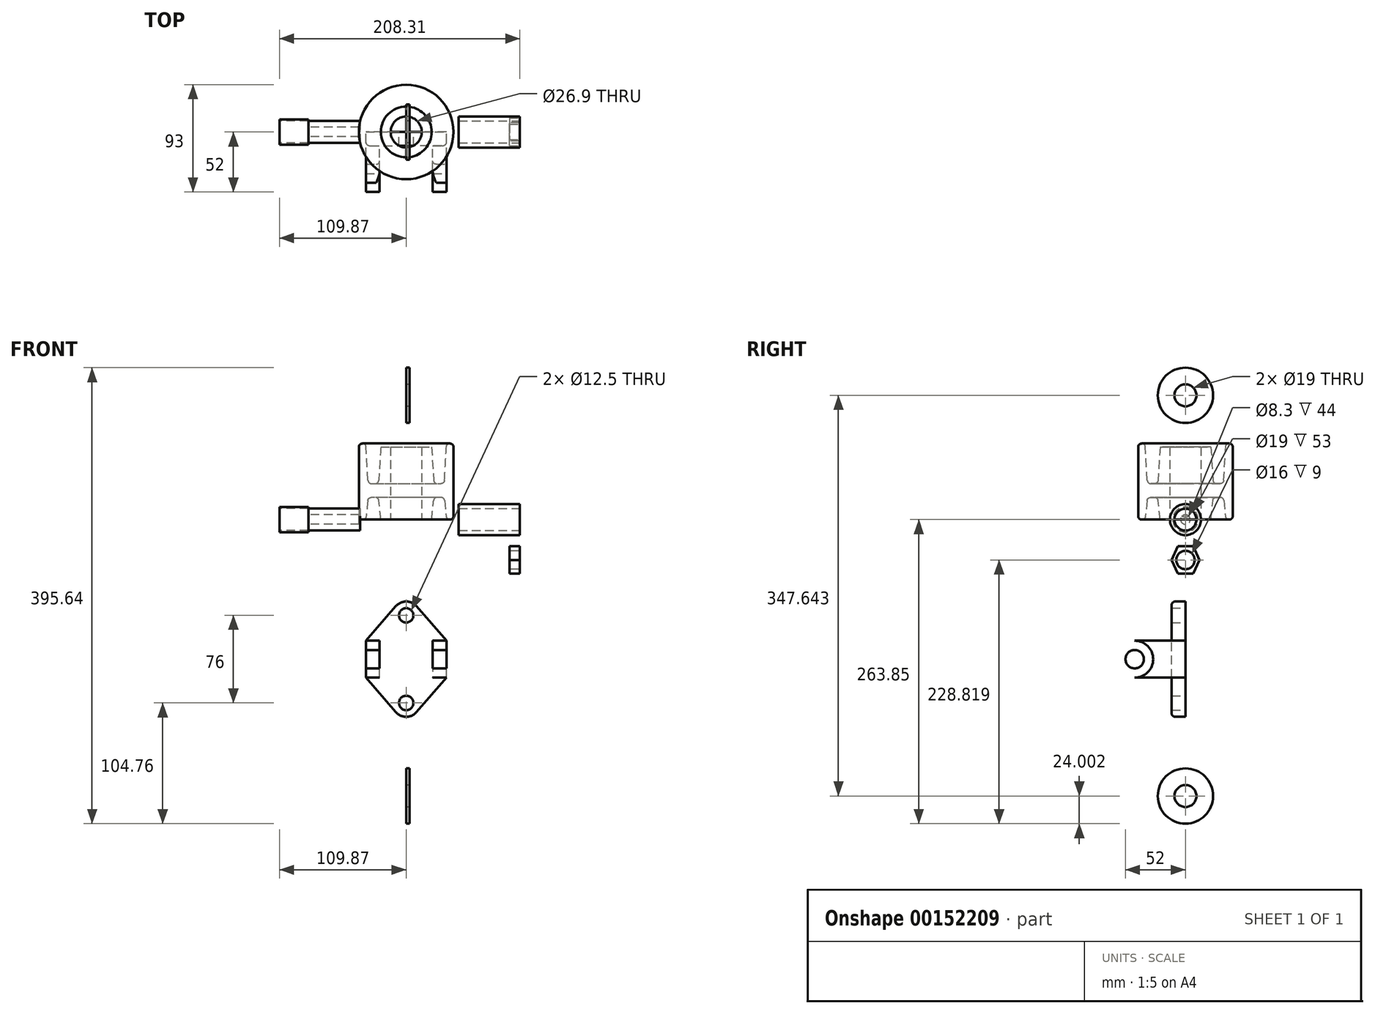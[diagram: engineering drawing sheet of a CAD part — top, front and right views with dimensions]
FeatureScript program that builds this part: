
annotation { "Feature Type Name" : "Feature", "Feature Type Description" : "" }
export const myFeature = defineFeature(function(context is Context, id is Id, definition is map)
    precondition{}
    {
        {
            var Q0;
            Q0=qCreatedBy(makeId("Front.planeOp"),FACE);
            var sketch = newSketch(context, id + "F0", { "sketchPlane" : qUnion([Q0])});
            skLineSegment(sketch, "E0", {"start": v(-13.45, 0) * mm, "end": v(-13.45, 63) * mm});
            skLineSegment(sketch, "E1", {"start": v(-13.45, 63) * mm, "end": v(-22, 63) * mm});
            skLineSegment(sketch, "E2", {"start": v(-22, 63) * mm, "end": v(-24, 31.2) * mm});
            skLineSegment(sketch, "E3", {"start": v(-24, 31.2) * mm, "end": v(-33, 31.2) * mm});
            skLineSegment(sketch, "E4", {"start": v(-33, 31.2) * mm, "end": v(-35, 66) * mm});
            skLineSegment(sketch, "E5", {"start": v(-35, 66) * mm, "end": v(-41, 66) * mm});
            skLineSegment(sketch, "E6", {"start": v(-41, 66) * mm, "end": v(-41, 0) * mm});
            skLineSegment(sketch, "E7", {"start": v(-41, 0) * mm, "end": v(-35, 0) * mm});
            skLineSegment(sketch, "E8", {"start": v(-35, 0) * mm, "end": v(-33, 19.2) * mm});
            skLineSegment(sketch, "E9", {"start": v(-33, 19.2) * mm, "end": v(-24, 19.2) * mm});
            skLineSegment(sketch, "E10", {"start": v(-24, 19.2) * mm, "end": v(-22, 0) * mm});
            skLineSegment(sketch, "E11", {"start": v(-22, 0) * mm, "end": v(-13.45, 0) * mm});
            skLineSegment(sketch, "E12", {"start": v(0, 0) * mm, "end": v(0, 72.33) * mm, "construction": true});
            skSolve(sketch);
        }
        {
            var Q0;
            Q0=qSketchRegion(id+"F0",true);
            var Q1;
            Q1=sQuery(id+"F0.wireOp",EDGE,"E12");
            revolve(context, id + "F1", {"entities" : qUnion([Q0]), "axis" : qUnion([Q1]), "revolveType" : RevolveType.FULL});
        }
        {
            var Q0;
            Q0=makeQuery(id+"F1.opRevolve","SWEPT_EDGE",EDGE,{"disambiguationData":[OSD([sQuery(id+"F0.wireOp",EDGE,"E5"),sQuery(id+"F0.wireOp",EDGE,"E6")])]});
            var Q1;
            Q1=makeQuery(id+"F1.opRevolve","SWEPT_EDGE",EDGE,{"disambiguationData":[OSD([sQuery(id+"F0.wireOp",EDGE,"E4"),sQuery(id+"F0.wireOp",EDGE,"E5")])]});
            var Q2;
            Q2=makeQuery(id+"F1.opRevolve","SWEPT_EDGE",EDGE,{"disambiguationData":[OSD([sQuery(id+"F0.wireOp",EDGE,"E2"),sQuery(id+"F0.wireOp",EDGE,"E3")])]});
            var Q3;
            Q3=makeQuery(id+"F1.opRevolve","SWEPT_FACE",FACE,{"disambiguationData":[OSD([sQuery(id+"F0.wireOp",EDGE,"E3")])]});
            var Q4;
            Q4=makeQuery(id+"F1.opRevolve","SWEPT_EDGE",EDGE,{"disambiguationData":[OSD([sQuery(id+"F0.wireOp",EDGE,"E6"),sQuery(id+"F0.wireOp",EDGE,"E7")])]});
            var Q5;
            Q5=makeQuery(id+"F1.opRevolve","SWEPT_EDGE",EDGE,{"disambiguationData":[OSD([sQuery(id+"F0.wireOp",EDGE,"E7"),sQuery(id+"F0.wireOp",EDGE,"E8")])]});
            fillet(context, id + "F2", {"entities" : qUnion([Q0, Q1, Q2, Q3, Q4, Q5]), "radius" : 3 * mm, "tangentPropagation" : true, "allowEdgeOverflow" : false});
        }
        {
            var Q0;
            Q0=makeQuery(id+"F1.opRevolve","SWEPT_EDGE",EDGE,{"disambiguationData":[OSD([sQuery(id+"F0.wireOp",EDGE,"E8"),sQuery(id+"F0.wireOp",EDGE,"E9")])]});
            var Q1;
            Q1=makeQuery(id+"F1.opRevolve","SWEPT_EDGE",EDGE,{"disambiguationData":[OSD([sQuery(id+"F0.wireOp",EDGE,"E9"),sQuery(id+"F0.wireOp",EDGE,"E10")])]});
            fillet(context, id + "F3", {"entities" : qUnion([Q0, Q1]), "radius" : 3 * mm, "tangentPropagation" : true, "allowEdgeOverflow" : false});
        }
        {
            var Q0;
            Q0=qCreatedBy(makeId("Front.planeOp"),FACE);
            var sketch = newSketch(context, id + "F4", { "sketchPlane" : qUnion([Q0])});
            skLineSegment(sketch, "E13", {"start": v(-35, -105.09) * mm, "end": v(-9.06, -75.22) * mm});
            skLineSegment(sketch, "E14", {"start": v(9.06, -75.22) * mm, "end": v(35, -105.09) * mm});
            skLineSegment(sketch, "E15", {"start": v(35, -105.09) * mm, "end": v(35, -137.09) * mm});
            skLineSegment(sketch, "E16", {"start": v(35, -137.09) * mm, "end": v(9.06, -166.96) * mm});
            skLineSegment(sketch, "E17", {"start": v(-9.06, -166.96) * mm, "end": v(-35, -137.09) * mm});
            skLineSegment(sketch, "E18", {"start": v(-35, -137.09) * mm, "end": v(-35, -105.09) * mm});
            skArc(sketch, "E19", {"start": v(-9.06, -75.22) * mm, "mid": v(0, -71.09) * mm, "end": v(9.06, -75.22) * mm});
            skArc(sketch, "E20", {"start": v(-9.06, -166.96) * mm, "mid": v(0, -171.09) * mm, "end": v(9.06, -166.96) * mm});
            skCircle(sketch, "E21", {"center": v(0, -83.09) * mm, "radius": 6.25 * mm});
            skCircle(sketch, "E22", {"center": v(0, -159.09) * mm, "radius": 6.25 * mm});
            skLineSegment(sketch, "E23", {"start": v(0, 0) * mm, "end": v(0, -228.96) * mm, "construction": true});
            skSolve(sketch);
        }
        {
            var Q0;
            Q0=qSketchRegion(id+"F4",true);
            extrude(context, id + "F5", {"entities" : qUnion([Q0]), "depth" : 12 * mm});
        }
        {
            var Q0;
            Q0=makeQuery(id+"F5.opExtrude","CAP_FACE",FACE,{"disambiguationData":[OSD([sQuery(id+"F4.wireOp",EDGE,"E13"),sQuery(id+"F4.wireOp",EDGE,"E14"),sQuery(id+"F4.wireOp",EDGE,"E15"),sQuery(id+"F4.wireOp",EDGE,"E16"),sQuery(id+"F4.wireOp",EDGE,"E17"),sQuery(id+"F4.wireOp",EDGE,"E18"),sQuery(id+"F4.wireOp",EDGE,"E19"),sQuery(id+"F4.wireOp",EDGE,"E20"),sQuery(id+"F4.wireOp",EDGE,"E21"),sQuery(id+"F4.wireOp",EDGE,"E22")])],"isStart":false});
            var sketch = newSketch(context, id + "F6", { "sketchPlane" : qUnion([Q0])});
            skLineSegment(sketch, "E24.0", {"start": v(35, -105.09) * mm, "end": v(35, -137.09) * mm});
            skLineSegment(sketch, "E25.0", {"start": v(-35, -137.09) * mm, "end": v(-35, -105.09) * mm});
            skLineSegment(sketch, "E26", {"start": v(-35, -105.09) * mm, "end": v(-23, -105.09) * mm});
            skLineSegment(sketch, "E27", {"start": v(-23, -105.09) * mm, "end": v(-23, -137.09) * mm});
            skLineSegment(sketch, "E28", {"start": v(-23, -137.09) * mm, "end": v(-35, -137.09) * mm});
            skLineSegment(sketch, "E29", {"start": v(35, -137.09) * mm, "end": v(23, -137.09) * mm});
            skLineSegment(sketch, "E30", {"start": v(23, -137.09) * mm, "end": v(23, -105.09) * mm});
            skLineSegment(sketch, "E31", {"start": v(23, -105.09) * mm, "end": v(35, -105.09) * mm});
            skSolve(sketch);
        }
        {
            var Q0;
            Q0=qSketchRegion(id+"F6",true);
            extrude(context, id + "F7", {"entities" : qUnion([Q0]), "operationType" : NewBodyOperationType.ADD, "depth" : 48 * mm});
        }
        {
            var Q0;
            Q0=makeQuery(id+"F7.boolean.opBoolean","MERGE",FACE,{"derivedFrom":[makeQuery(id+"F5.opExtrude","SWEPT_FACE",FACE,{"disambiguationData":[OSD([sQuery(id+"F4.wireOp",EDGE,"E15")])]}),makeQuery(id+"F7.opExtrude","SWEPT_FACE",FACE,{"disambiguationData":[OSD([sQuery(id+"F6.wireOp",EDGE,"E24.0")])]})]});
            var sketch = newSketch(context, id + "F8", { "sketchPlane" : qUnion([Q0])});
            skLineSegment(sketch, "E32.0", {"start": v(-60, -137.09) * mm, "end": v(-12, -137.09) * mm});
            skLineSegment(sketch, "E33.0", {"start": v(-60, -105.09) * mm, "end": v(-12, -105.09) * mm});
            skArc(sketch, "E34", {"start": v(-44, -105.09) * mm, "mid": v(-60, -121.09) * mm, "end": v(-44, -137.09) * mm});
            skLineSegment(sketch, "E35.0", {"start": v(-60, -105.09) * mm, "end": v(-60, -137.09) * mm});
            skCircle(sketch, "E36", {"center": v(-44, -121.09) * mm, "radius": 8 * mm});
            skSolve(sketch);
        }
        {
            var Q0;
            Q0=qSketchRegion(id+"F8",true);
            extrude(context, id + "F9", {"entities" : qUnion([Q0]), "operationType" : NewBodyOperationType.REMOVE, "oppositeDirection" : true, "depth" : 172.56 * mm});
        }
        {
            var Q0;
            Q0=qCreatedBy(makeId("Right.planeOp"),FACE);
            var sketch = newSketch(context, id + "F10", { "sketchPlane" : qUnion([Q0])});
            skCircle(sketch, "E37", {"center": v(0, 107.8) * mm, "radius": 9.5 * mm});
            skCircle(sketch, "E38", {"center": v(0, 107.8) * mm, "radius": 24 * mm});
            skSolve(sketch);
        }
        {
            var Q0;
            Q0=qSketchRegion(id+"F10",true);
            extrude(context, id + "F11", {"entities" : qUnion([Q0]), "depth" : 3 * mm});
        }
        {
            var Q0;
            {var subQ0=sQuery(id+"F8.wireOp",EDGE,"E34");var subQ1=makeQuery(id+"F8.imprint","INTERSECT",VERTEX,{"derivedFrom":[subQ0,sQuery(id+"F8.wireOp",EDGE,"E35.0")]});Q0=makeQuery(id+"F9.boolean.opBoolean","INTERSECT",EDGE,{"derivedFrom":[makeQuery(id+"F7.opExtrude","SWEPT_FACE",FACE,{"disambiguationData":[OSD([sQuery(id+"F6.wireOp",EDGE,"E27")])]}),makeQuery(id+"F9.opExtrude","SWEPT_FACE",FACE,{"disambiguationData":[OSD([subQ0]),TDD([makeQuery(id+"F8.imprint","IMPRINT",EDGE,{"disambiguationData":[TD([[subQ1,-1.0]])],"derivedFrom":subQ0})])]}),makeQuery(id+"F9.opExtrude","SWEPT_FACE",FACE,{"disambiguationData":[OSD([subQ0]),TDD([makeQuery(id+"F8.imprint","IMPRINT",EDGE,{"disambiguationData":[TD([[subQ1,1.0]])],"derivedFrom":subQ0})])]})]});}
            var Q1;
            Q1=makeQuery(id+"F7.opExtrude","CAP_EDGE",EDGE,{"disambiguationData":[OSD([sQuery(id+"F6.wireOp",EDGE,"E27")])],"isStart":true});
            var Q2;
            {var subQ0=sQuery(id+"F8.wireOp",EDGE,"E34");var subQ1=makeQuery(id+"F8.imprint","INTERSECT",VERTEX,{"derivedFrom":[subQ0,sQuery(id+"F8.wireOp",EDGE,"E35.0")]});Q2=makeQuery(id+"F9.boolean.opBoolean","INTERSECT",EDGE,{"derivedFrom":[makeQuery(id+"F7.opExtrude","SWEPT_FACE",FACE,{"disambiguationData":[OSD([sQuery(id+"F6.wireOp",EDGE,"E30")])]}),makeQuery(id+"F9.opExtrude","SWEPT_FACE",FACE,{"disambiguationData":[OSD([subQ0]),TDD([makeQuery(id+"F8.imprint","IMPRINT",EDGE,{"disambiguationData":[TD([[subQ1,-1.0]])],"derivedFrom":subQ0})])]}),makeQuery(id+"F9.opExtrude","SWEPT_FACE",FACE,{"disambiguationData":[OSD([subQ0]),TDD([makeQuery(id+"F8.imprint","IMPRINT",EDGE,{"disambiguationData":[TD([[subQ1,1.0]])],"derivedFrom":subQ0})])]})]});}
            var Q3;
            Q3=makeQuery(id+"F7.opExtrude","CAP_EDGE",EDGE,{"disambiguationData":[OSD([sQuery(id+"F6.wireOp",EDGE,"E30")])],"isStart":true});
            fillet(context, id + "F12", {"entities" : qUnion([Q0, Q1, Q2, Q3]), "radius" : 3 * mm, "tangentPropagation" : true, "allowEdgeOverflow" : false});
        }
        {
            var Q0;
            Q0=makeQuery(id+"F5.opExtrude","CAP_EDGE",EDGE,{"disambiguationData":[OSD([sQuery(id+"F4.wireOp",EDGE,"E13")])],"isStart":false});
            var Q1;
            Q1=makeQuery(id+"F5.opExtrude","CAP_EDGE",EDGE,{"disambiguationData":[OSD([sQuery(id+"F4.wireOp",EDGE,"E17")])],"isStart":false});
            fillet(context, id + "F13", {"entities" : qUnion([Q0, Q1]), "radius" : 3 * mm, "tangentPropagation" : true, "allowEdgeOverflow" : false});
        }
        {
            var Q0;
            Q0=qCreatedBy(makeId("Front.planeOp"),FACE);
            var sketch = newSketch(context, id + "F14", { "sketchPlane" : qUnion([Q0])});
            skLineSegment(sketch, "E39", {"start": v(-109.87, 0) * mm, "end": v(98.44, 0) * mm, "construction": true});
            skSolve(sketch);
        }
        {
            var Q0;
            Q0=sQuery(id+"F14.wireOp",VERTEX,"E39.end");
            var Q1;
            Q1=qCreatedBy(makeId("Right.planeOp"),FACE);
            cPlane(context, id + "F15", {"entities" : qUnion([Q0, Q1]), "cplaneType" : CPlaneType.PLANE_POINT, "offset" : 25 * mm, "width" : 150 * mm, "height" : 150 * mm});
        }
        {
            var Q0;
            Q0=qCreatedBy(id+"F15.planeOp",FACE);
            var sketch = newSketch(context, id + "F16", { "sketchPlane" : qUnion([Q0])});
            skCircle(sketch, "E40", {"center": v(0, 0) * mm, "radius": 9.5 * mm});
            skCircle(sketch, "E41", {"center": v(0, 0) * mm, "radius": 13.45 * mm});
            skSolve(sketch);
        }
        {
            var Q0;
            Q0=qSketchRegion(id+"F16",true);
            extrude(context, id + "F17", {"entities" : qUnion([Q0]), "oppositeDirection" : true, "depth" : 53 * mm});
        }
        {
            var Q0;
            Q0=sQuery(id+"F14.wireOp",VERTEX,"E39.start");
            var Q1;
            Q1=qCreatedBy(makeId("Right.planeOp"),FACE);
            cPlane(context, id + "F18", {"entities" : qUnion([Q0, Q1]), "cplaneType" : CPlaneType.PLANE_POINT, "offset" : 25 * mm, "width" : 150 * mm, "height" : 150 * mm});
        }
        {
            var Q0;
            Q0=qCreatedBy(id+"F18.planeOp",FACE);
            var sketch = newSketch(context, id + "F19", { "sketchPlane" : qUnion([Q0])});
            skCircle(sketch, "E42", {"center": v(0, 0) * mm, "radius": 11 * mm});
            skSolve(sketch);
        }
        {
            var Q0;
            Q0=qSketchRegion(id+"F19",true);
            extrude(context, id + "F20", {"entities" : qUnion([Q0]), "depth" : 25 * mm});
        }
        {
            var Q0;
            Q0=qCreatedBy(id+"F18.planeOp",FACE);
            var sketch = newSketch(context, id + "F21", { "sketchPlane" : qUnion([Q0])});
            skCircle(sketch, "E43", {"center": v(0, 0) * mm, "radius": 9.5 * mm});
            skSolve(sketch);
        }
        {
            var Q0;
            Q0=qSketchRegion(id+"F21",true);
            extrude(context, id + "F22", {"entities" : qUnion([Q0]), "depth" : 70 * mm});
        }
        {
            var Q0;
            Q0=makeQuery(id+"F20.opExtrude","CAP_FACE",FACE,{"disambiguationData":[OSD([sQuery(id+"F19.wireOp",EDGE,"E42")])],"isStart":false});
            var sketch = newSketch(context, id + "F23", { "sketchPlane" : qUnion([Q0])});
            skCircle(sketch, "E44", {"center": v(0, 0) * mm, "radius": 4.15 * mm});
            skSolve(sketch);
        }
        {
            var Q0;
            Q0=qSketchRegion(id+"F23",true);
            extrude(context, id + "F24", {"entities" : qUnion([Q0]), "operationType" : NewBodyOperationType.REMOVE, "depth" : 44 * mm});
        }
        {
            var Q0;
            Q0=qCreatedBy(id+"F15.planeOp",FACE);
            var sketch = newSketch(context, id + "F25", { "sketchPlane" : qUnion([Q0])});
            skLineSegment(sketch, "E45", {"start": v(0, -23.03) * mm, "end": v(0, -47.03) * mm, "construction": true});
            skLineSegment(sketch, "E46", {"start": v(-12, -35.03) * mm, "end": v(12, -35.03) * mm, "construction": true});
            skPoint(sketch, "E46.startSnap0", {"position": v(0, -35.03) * mm});
            skLineSegment(sketch, "E47", {"start": v(-12, -35.03) * mm, "end": v(-6.58, -23.03) * mm});
            skLineSegment(sketch, "E48", {"start": v(-6.58, -23.03) * mm, "end": v(6.58, -23.03) * mm});
            skLineSegment(sketch, "E49", {"start": v(6.58, -23.03) * mm, "end": v(12, -35.03) * mm});
            skLineSegment(sketch, "E50", {"start": v(12, -35.03) * mm, "end": v(6.58, -47.03) * mm});
            skLineSegment(sketch, "E51", {"start": v(6.58, -47.03) * mm, "end": v(-6.58, -47.03) * mm});
            skLineSegment(sketch, "E52", {"start": v(-6.58, -47.03) * mm, "end": v(-12, -35.03) * mm});
            skSolve(sketch);
        }
        {
            var Q0;
            Q0=qSketchRegion(id+"F25",true);
            extrude(context, id + "F26", {"entities" : qUnion([Q0]), "oppositeDirection" : true, "depth" : 9 * mm});
        }
        {
            var Q0;
            Q0=makeQuery(id+"F26.opExtrude","CAP_FACE",FACE,{"disambiguationData":[OSD([sQuery(id+"F25.wireOp",EDGE,"E47"),sQuery(id+"F25.wireOp",EDGE,"E48"),sQuery(id+"F25.wireOp",EDGE,"E49"),sQuery(id+"F25.wireOp",EDGE,"E50"),sQuery(id+"F25.wireOp",EDGE,"E51"),sQuery(id+"F25.wireOp",EDGE,"E52")])],"isStart":true});
            var sketch = newSketch(context, id + "F27", { "sketchPlane" : qUnion([Q0])});
            skCircle(sketch, "E53", {"center": v(0, -35.03) * mm, "radius": 8 * mm});
            skPoint(sketch, "E53.centerSnap0", {"position": v(0, -23.03) * mm});
            skSolve(sketch);
        }
        {
            var Q0;
            Q0=qSketchRegion(id+"F27",true);
            extrude(context, id + "F28", {"entities" : qUnion([Q0]), "operationType" : NewBodyOperationType.REMOVE, "depth" : 10 * mm, "hasSecondDirection" : true, "secondDirectionOppositeDirection" : true, "secondDirectionDepth" : 10 * mm});
        }
        {
            var Q0;
            Q0=qCreatedBy(makeId("Front.planeOp"),FACE);
            var sketch = newSketch(context, id + "F29", { "sketchPlane" : qUnion([Q0])});
            skLineSegment(sketch, "E54", {"start": v(0, 178.4) * mm, "end": v(0, -284.12) * mm, "construction": true});
            skSolve(sketch);
        }
        {
            var Q0;
            Q0=sQuery(id+"F29.wireOp",VERTEX,"E54.end");
            var Q1;
            Q1=qCreatedBy(makeId("Right.planeOp"),FACE);
            cPlane(context, id + "F30", {"entities" : qUnion([Q0, Q1]), "cplaneType" : CPlaneType.PLANE_POINT, "offset" : 25 * mm, "width" : 150 * mm, "height" : 150 * mm});
        }
        {
            var Q0;
            Q0=qCreatedBy(id+"F30.planeOp",FACE);
            var sketch = newSketch(context, id + "F31", { "sketchPlane" : qUnion([Q0])});
            skCircle(sketch, "E55", {"center": v(0, -239.85) * mm, "radius": 24 * mm});
            skCircle(sketch, "E56", {"center": v(0, -239.85) * mm, "radius": 9.5 * mm});
            skSolve(sketch);
        }
        {
            var Q0;
            Q0=qSketchRegion(id+"F31",true);
            extrude(context, id + "F32", {"entities" : qUnion([Q0]), "depth" : 3 * mm});
        }
    });
